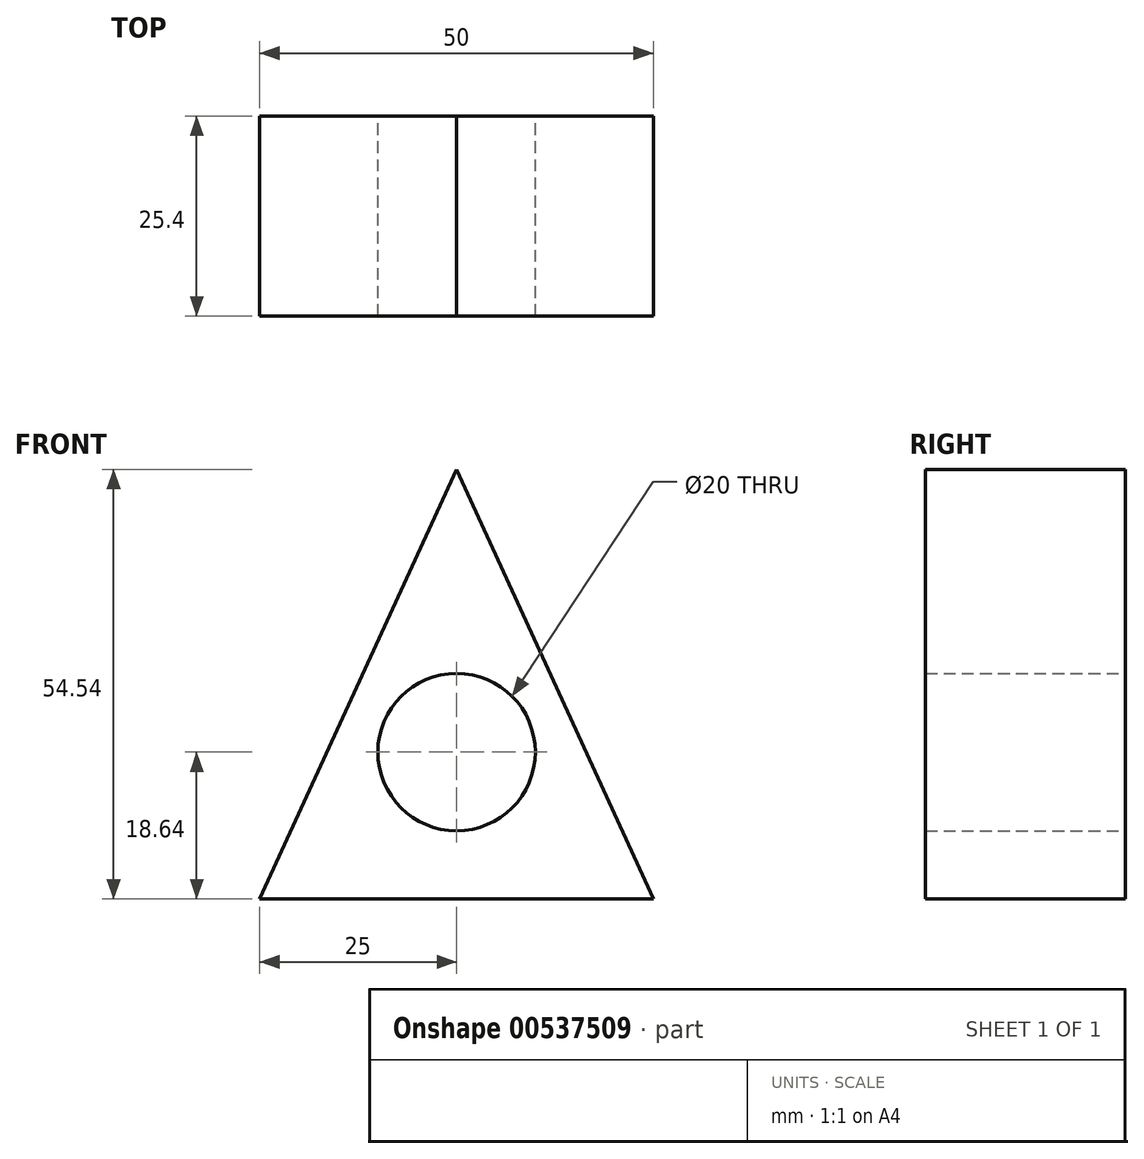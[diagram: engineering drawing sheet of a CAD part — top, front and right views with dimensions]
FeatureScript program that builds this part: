
annotation { "Feature Type Name" : "Feature", "Feature Type Description" : "" }
export const myFeature = defineFeature(function(context is Context, id is Id, definition is map)
    precondition{}
    {
        {
            var Q0;
            Q0=qCreatedBy(makeId("Front.planeOp"),FACE);
            var sketch = newSketch(context, id + "F0", { "sketchPlane" : qUnion([Q0])});
            skLineSegment(sketch, "E0", {"start": v(-25, -18.64) * mm, "end": v(25, -18.64) * mm});
            skLineSegment(sketch, "E1", {"start": v(25, -18.64) * mm, "end": v(0, 35.9) * mm});
            skLineSegment(sketch, "E2", {"start": v(0, 35.9) * mm, "end": v(-25, -18.64) * mm});
            skCircle(sketch, "E3", {"center": v(0, 0) * mm, "radius": 10 * mm});
            skSolve(sketch);
        }
        {
            var Q0;
            Q0 = qSketchRegion(id + "F0", true);
            extrude(context, id + "F1", {"entities" : qUnion([Q0]), "depth" : 25.4 * mm, "offsetDistance" : 25.4 * mm});
        }
    });
